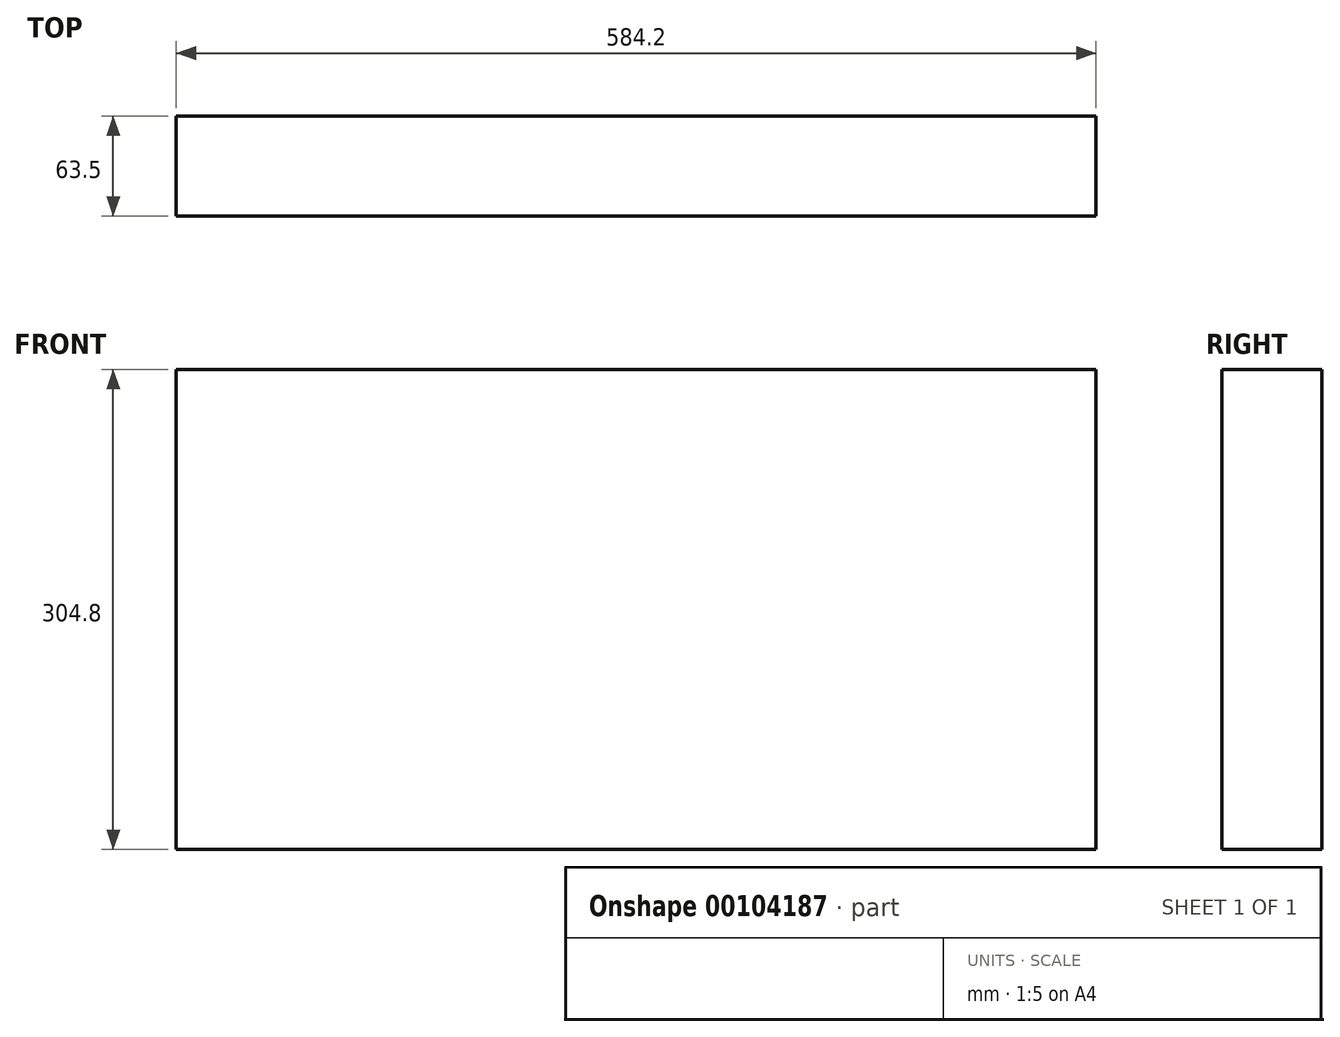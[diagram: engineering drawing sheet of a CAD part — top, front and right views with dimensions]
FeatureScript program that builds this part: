
annotation { "Feature Type Name" : "Feature", "Feature Type Description" : "" }
export const myFeature = defineFeature(function(context is Context, id is Id, definition is map)
    precondition{}
    {
        {
            var Q0;
            Q0=qCreatedBy(makeId("Top.planeOp"),FACE);
            var sketch = newSketch(context, id + "F0", { "sketchPlane" : qUnion([Q0])});
            skLineSegment(sketch, "E0.bottom", {"start": v(-300.6, -18.23) * mm, "end": v(283.6, -18.23) * mm});
            skLineSegment(sketch, "E0.top", {"start": v(-300.6, -81.73) * mm, "end": v(283.6, -81.73) * mm});
            skLineSegment(sketch, "E0.left", {"start": v(-300.6, -18.23) * mm, "end": v(-300.6, -81.73) * mm});
            skLineSegment(sketch, "E0.right", {"start": v(283.6, -18.23) * mm, "end": v(283.6, -81.73) * mm});
            skSolve(sketch);
        }
        {
            var Q0;
            Q0 = qSketchRegion(id + "F0", true);
            extrude(context, id + "F1", {"entities" : qUnion([Q0]), "depth" : 304.8 * mm});
        }
    });
